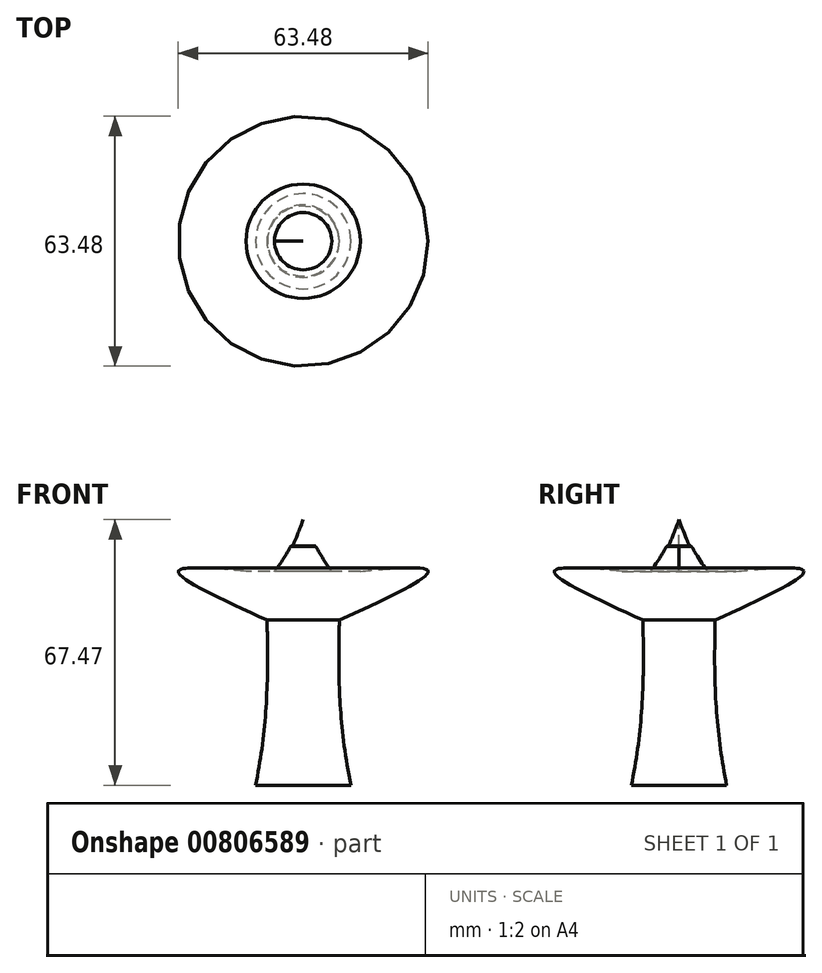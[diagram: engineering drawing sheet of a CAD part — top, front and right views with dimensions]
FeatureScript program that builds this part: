
annotation { "Feature Type Name" : "Feature", "Feature Type Description" : "" }
export const myFeature = defineFeature(function(context is Context, id is Id, definition is map)
    precondition{}
    {
        {
            var Q0;
            Q0=qCreatedBy(makeId("Front.planeOp"),FACE);
            var sketch = newSketch(context, id + "F0", { "sketchPlane" : qUnion([Q0])});
            skLineSegment(sketch, "E0", {"start": v(0, 0) * mm, "end": v(-14.52, 0) * mm});
            skFitSpline(sketch, "E1", {"points": [v(-14.52, 0) * mm, v(-9.2, -12.42) * mm, v(-12.1, -54.36) * mm], "startDerivative": vector(42.62, -23.34) * mm, "endDerivative": vector(-16.7, -81.5) * mm});
            skFitSpline(sketch, "E2", {"points": [v(-7.26, 0) * mm, v(-3.1, 6.35) * mm, v(0, 13.1) * mm], "startDerivative": vector(16.52, 21.53) * mm, "endDerivative": vector(18.97, 51.13) * mm});
            skFitSpline(sketch, "E3", {"points": [v(-12.1, -54.36) * mm, v(0, -54.36) * mm], "startDerivative": vector(12.1, 0) * mm, "endDerivative": vector(12.1, 0) * mm});
            skLineSegment(sketch, "E4", {"start": v(0, 13.1) * mm, "end": v(0, -54.36) * mm});
            skFitSpline(sketch, "E5", {"points": [v(-14.52, 0) * mm, v(-31.73, 0) * mm, v(-9.2, -12.42) * mm], "startDerivative": vector(-56.07, 5.08) * mm, "endDerivative": vector(62.75, -28.8) * mm});
            skLineSegment(sketch, "E6", {"start": v(-9.12, -27.55) * mm, "end": v(0, -27.55) * mm});
            skSolve(sketch);
        }
        {
            var Q0;
            {var subQ1=sQuery(id+"F0.wireOp",EDGE,"E1");Q0=makeQuery(id+"F0.imprint","IMPRINT",FACE,{"disambiguationData":[TD([[makeQuery(id+"F0.imprint","IMPRINT",EDGE,{"derivedFrom":subQ1}),1.0]])]});}
            var Q1;
            Q1=sQuery(id+"F0.wireOp",EDGE,"E4");
            revolve(context, id + "F1", {"surfaceOperationType" : NewSurfaceOperationType.NEW, "entities" : qUnion([Q0]), "axis" : qUnion([Q1]), "revolveType" : RevolveType.FULL});
        }
        {
            var Q0;
            {var subQ3=sQuery(id+"F0.wireOp",EDGE,"E2");Q0=makeQuery(id+"F0.imprint","IMPRINT",FACE,{"disambiguationData":[TD([[makeQuery(id+"F0.imprint","IMPRINT",EDGE,{"derivedFrom":subQ3}),-1.0]])]});}
            var Q1;
            Q1=sQuery(id+"F0.wireOp",EDGE,"E4");
            revolve(context, id + "F2", {"operationType" : NewBodyOperationType.ADD, "surfaceOperationType" : NewSurfaceOperationType.NEW, "entities" : qUnion([Q0]), "axis" : qUnion([Q1]), "revolveType" : RevolveType.FULL});
        }
        {
            var Q0;
            {var subQ0=sQuery(id+"F0.wireOp",EDGE,"E5");Q0=makeQuery(id+"F0.imprint","IMPRINT",FACE,{"disambiguationData":[TD([[makeQuery(id+"F0.imprint","IMPRINT",EDGE,{"derivedFrom":subQ0}),1.0]])]});}
            var Q1;
            Q1=sQuery(id+"F0.wireOp",EDGE,"E4");
            revolve(context, id + "F3", {"operationType" : NewBodyOperationType.ADD, "surfaceOperationType" : NewSurfaceOperationType.NEW, "entities" : qUnion([Q0]), "axis" : qUnion([Q1]), "revolveType" : RevolveType.FULL});
        }
        {
            var Q0;
            {var subQ0=sQuery(id+"F0.wireOp",EDGE,"E3");Q0=makeQuery(id+"F0.imprint","IMPRINT",FACE,{"disambiguationData":[TD([[makeQuery(id+"F0.imprint","IMPRINT",EDGE,{"derivedFrom":subQ0}),1.0]])]});}
            var Q1;
            Q1=sQuery(id+"F0.wireOp",EDGE,"E4");
            revolve(context, id + "F4", {"operationType" : NewBodyOperationType.ADD, "surfaceOperationType" : NewSurfaceOperationType.NEW, "entities" : qUnion([Q0]), "axis" : qUnion([Q1]), "revolveType" : RevolveType.FULL});
        }
    });
